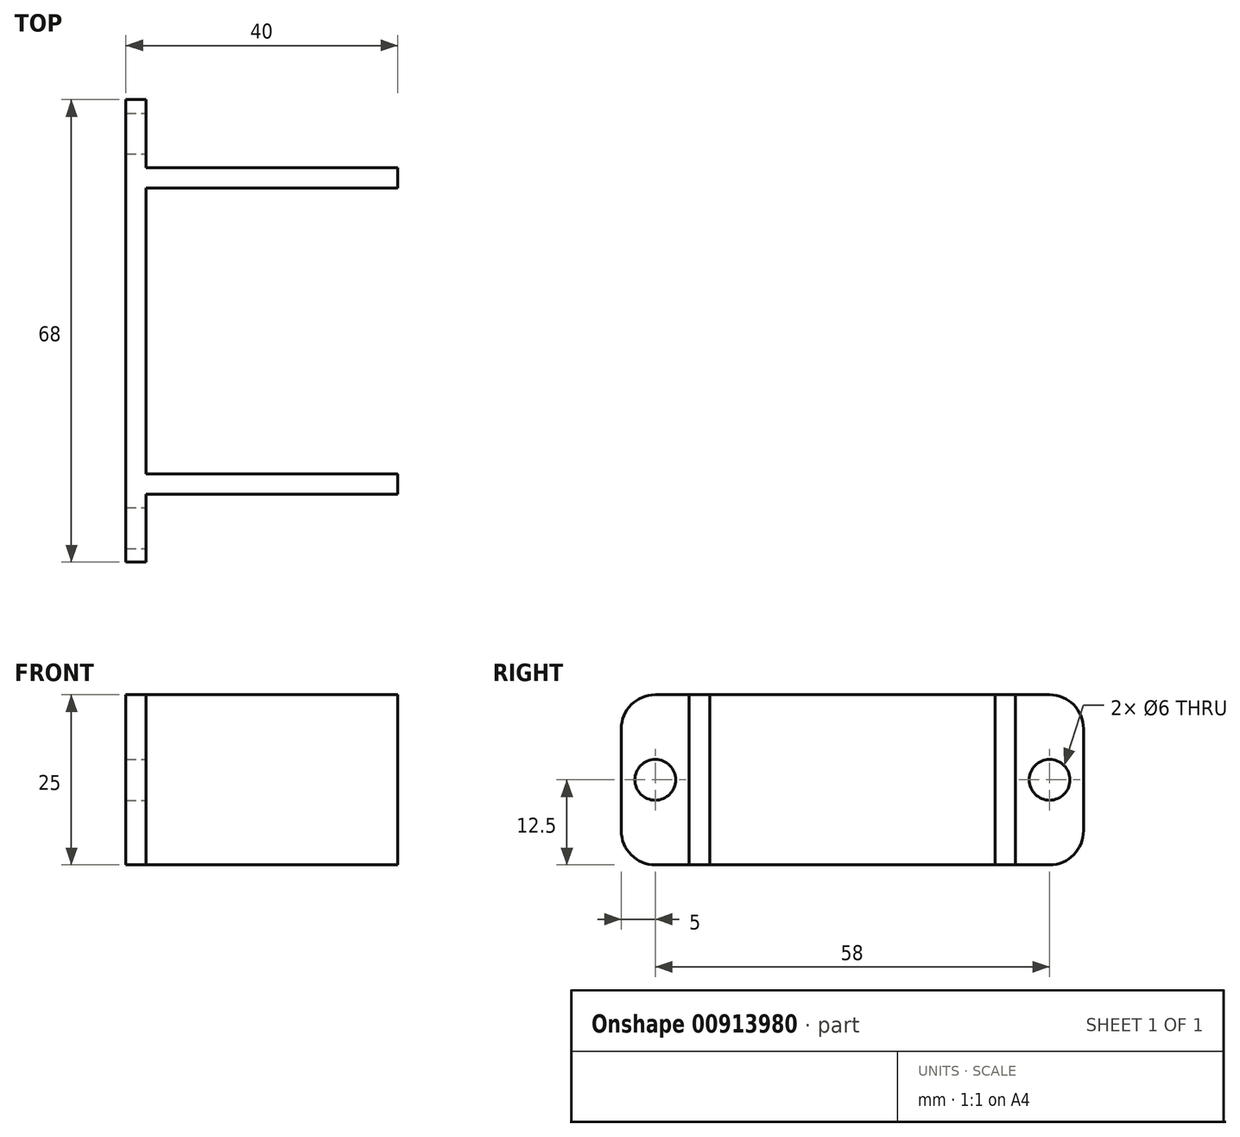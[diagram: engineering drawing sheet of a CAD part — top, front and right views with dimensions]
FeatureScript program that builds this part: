
annotation { "Feature Type Name" : "Feature", "Feature Type Description" : "" }
export const myFeature = defineFeature(function(context is Context, id is Id, definition is map)
    precondition{}
    {
        {
            var Q0;
            Q0=qCreatedBy(makeId("Top.planeOp"),FACE);
            var sketch = newSketch(context, id + "F0", { "sketchPlane" : qUnion([Q0])});
            skLineSegment(sketch, "E0.bottom", {"start": v(20, -24) * mm, "end": v(-20, -24) * mm});
            skLineSegment(sketch, "E0.top", {"start": v(20, 24) * mm, "end": v(-20, 24) * mm});
            skLineSegment(sketch, "E0.left", {"start": v(20, -24) * mm, "end": v(20, 24) * mm});
            skLineSegment(sketch, "E0.right", {"start": v(-20, -24) * mm, "end": v(-20, 24) * mm});
            skPoint(sketch, "E0.middle", {"position": v(0, 0) * mm});
            skSolve(sketch);
        }
        {
            var Q0;
            Q0=makeQuery(id+"F0.imprint","IMPRINT",FACE,{"disambiguationData":[TD([[makeQuery(id+"F0.imprint","IMPRINT",EDGE,{"derivedFrom":sQuery(id+"F0.wireOp",EDGE,"E0.bottom")}),-1.0]])]});
            extrude(context, id + "F1", {"entities" : qUnion([Q0]), "depth" : 25 * mm, "offsetDistance" : 25 * mm});
        }
        {
            var Q0;
            Q0=makeQuery(id+"F1.opExtrude","SWEPT_FACE",FACE,{"disambiguationData":[OSD([sQuery(id+"F0.wireOp",EDGE,"E0.bottom")])]});
            var sketch = newSketch(context, id + "F2", { "sketchPlane" : qUnion([Q0])});
            skLineSegment(sketch, "E1", {"start": v(-20, 25) * mm, "end": v(-17, 25) * mm});
            skLineSegment(sketch, "E2", {"start": v(-17, 25) * mm, "end": v(-17, 0) * mm});
            skLineSegment(sketch, "E3", {"start": v(20, 25) * mm, "end": v(17, 25) * mm});
            skLineSegment(sketch, "E4", {"start": v(17, 25) * mm, "end": v(17, 0) * mm});
            skSolve(sketch);
        }
        {
            var Q0;
            Q0=makeQuery(id+"F1.opExtrude","SWEPT_FACE",FACE,{"disambiguationData":[OSD([sQuery(id+"F0.wireOp",EDGE,"E0.left")])]});
            var sketch = newSketch(context, id + "F3", { "sketchPlane" : qUnion([Q0])});
            skLineSegment(sketch, "E5", {"start": v(-24, 25) * mm, "end": v(-21, 25) * mm});
            skLineSegment(sketch, "E6", {"start": v(-21, 25) * mm, "end": v(-21, 0) * mm});
            skLineSegment(sketch, "E7", {"start": v(24, 25) * mm, "end": v(21, 25) * mm});
            skLineSegment(sketch, "E8", {"start": v(21, 25) * mm, "end": v(21, 0) * mm});
            skSolve(sketch);
        }
        {
            var Q0;
            {var subQ0=sQuery(id+"F3.wireOp",EDGE,"E6");Q0=makeQuery(id+"F3.imprint","IMPRINT",FACE,{"disambiguationData":[TD([[makeQuery(id+"F3.imprint","IMPRINT",EDGE,{"derivedFrom":subQ0}),1.0]])]});}
            extrude(context, id + "F4", {"entities" : qUnion([Q0]), "operationType" : NewBodyOperationType.REMOVE, "oppositeDirection" : true, "depth" : 37 * mm, "offsetDistance" : 25 * mm});
        }
        {
            var Q0;
            Q0=makeQuery(id+"F2.imprint","IMPRINT",FACE,{"disambiguationData":[TD([[makeQuery(id+"F2.imprint","IMPRINT",EDGE,{"derivedFrom":sQuery(id+"F2.wireOp",EDGE,"E1")}),1.0]])]});
            extrude(context, id + "F5", {"entities" : qUnion([Q0]), "operationType" : NewBodyOperationType.ADD, "depth" : 10 * mm, "offsetDistance" : 25 * mm});
        }
        {
            var Q0;
            Q0=makeQuery(id+"F1.opExtrude","SWEPT_FACE",FACE,{"disambiguationData":[OSD([sQuery(id+"F0.wireOp",EDGE,"E0.top")])]});
            var sketch = newSketch(context, id + "F6", { "sketchPlane" : qUnion([Q0])});
            skLineSegment(sketch, "E9", {"start": v(20, 0) * mm, "end": v(17, 0) * mm});
            skLineSegment(sketch, "E10", {"start": v(17, 0) * mm, "end": v(17, 25) * mm});
            skSolve(sketch);
        }
        {
            var Q0;
            Q0=makeQuery(id+"F6.imprint","IMPRINT",FACE,{"disambiguationData":[TD([[makeQuery(id+"F6.imprint","IMPRINT",EDGE,{"derivedFrom":sQuery(id+"F6.wireOp",EDGE,"E9")}),1.0]])]});
            extrude(context, id + "F7", {"entities" : qUnion([Q0]), "operationType" : NewBodyOperationType.ADD, "depth" : 10 * mm, "offsetDistance" : 25 * mm});
        }
        {
            var Q0;
            Q0=makeQuery(id+"F7.opExtrude","CAP_EDGE",EDGE,{"disambiguationData":[OSD([sQuery(id+"F6.wireOp",EDGE,"E9")])],"isStart":false});
            var Q1;
            Q1=makeQuery(id+"F7.opExtrude","CAP_EDGE",EDGE,{"disambiguationData":[OSD([sQuery(id+"F0.wireOp",EDGE,"E0.top")])],"isStart":false});
            var Q2;
            Q2=makeQuery(id+"F5.opExtrude","CAP_EDGE",EDGE,{"disambiguationData":[OSD([sQuery(id+"F0.wireOp",EDGE,"E0.bottom")])],"isStart":false});
            var Q3;
            Q3=makeQuery(id+"F5.opExtrude","CAP_EDGE",EDGE,{"disambiguationData":[OSD([sQuery(id+"F2.wireOp",EDGE,"E1")])],"isStart":false});
            fillet(context, id + "F8", {"entities" : qUnion([Q0, Q1, Q2, Q3]), "radius" : 5 * mm, "tangentPropagation" : true, "allowEdgeOverflow" : false});
        }
        {
            var Q0;
            Q0=makeQuery(id+"F5.opExtrude","SWEPT_FACE",FACE,{"disambiguationData":[OSD([sQuery(id+"F2.wireOp",EDGE,"E2")])]});
            var sketch = newSketch(context, id + "F9", { "sketchPlane" : qUnion([Q0])});
            skLineSegment(sketch, "E11", {"start": v(-29, 0) * mm, "end": v(-29, 25) * mm});
            skCircle(sketch, "E12", {"center": v(-29, 12.5) * mm, "radius": 3 * mm});
            skSolve(sketch);
        }
        {
            var Q0;
            Q0=makeQuery(id+"F7.opExtrude","SWEPT_FACE",FACE,{"disambiguationData":[OSD([sQuery(id+"F6.wireOp",EDGE,"E10")])]});
            var sketch = newSketch(context, id + "F10", { "sketchPlane" : qUnion([Q0])});
            skLineSegment(sketch, "E13", {"start": v(29, 0) * mm, "end": v(29, 25) * mm});
            skCircle(sketch, "E14", {"center": v(29, 12.5) * mm, "radius": 3 * mm});
            skSolve(sketch);
        }
        {
            var Q0;
            {var subQ0=sQuery(id+"F10.wireOp",EDGE,"E14");var subQ1=sQuery(id+"F10.wireOp",EDGE,"E13");var subQ2=makeQuery(id+"F10.imprint","INTERSECT",VERTEX,{"disambiguationData":[OD(0.0)],"derivedFrom":[subQ1,subQ0]});Q0=makeQuery(id+"F10.imprint","IMPRINT",FACE,{"disambiguationData":[TD([[makeQuery(id+"F10.imprint","IMPRINT",EDGE,{"disambiguationData":[TD([[subQ2,-1.0]])],"derivedFrom":subQ1}),1.0]])]});}
            var Q1;
            {var subQ0=sQuery(id+"F10.wireOp",EDGE,"E14");var subQ1=sQuery(id+"F10.wireOp",EDGE,"E13");var subQ2=makeQuery(id+"F10.imprint","INTERSECT",VERTEX,{"disambiguationData":[OD(0.0)],"derivedFrom":[subQ1,subQ0]});Q1=makeQuery(id+"F10.imprint","IMPRINT",FACE,{"disambiguationData":[TD([[makeQuery(id+"F10.imprint","IMPRINT",EDGE,{"disambiguationData":[TD([[subQ2,-1.0]])],"derivedFrom":subQ1}),-1.0]])]});}
            var Q2;
            {var subQ0=sQuery(id+"F9.wireOp",EDGE,"E12");var subQ1=sQuery(id+"F9.wireOp",EDGE,"E11");var subQ2=makeQuery(id+"F9.imprint","INTERSECT",VERTEX,{"disambiguationData":[OD(0.0)],"derivedFrom":[subQ1,subQ0]});Q2=makeQuery(id+"F9.imprint","IMPRINT",FACE,{"disambiguationData":[TD([[makeQuery(id+"F9.imprint","IMPRINT",EDGE,{"disambiguationData":[TD([[subQ2,-1.0]])],"derivedFrom":subQ1}),1.0]])]});}
            var Q3;
            {var subQ0=sQuery(id+"F9.wireOp",EDGE,"E12");var subQ1=sQuery(id+"F9.wireOp",EDGE,"E11");var subQ2=makeQuery(id+"F9.imprint","INTERSECT",VERTEX,{"disambiguationData":[OD(0.0)],"derivedFrom":[subQ1,subQ0]});Q3=makeQuery(id+"F9.imprint","IMPRINT",FACE,{"disambiguationData":[TD([[makeQuery(id+"F9.imprint","IMPRINT",EDGE,{"disambiguationData":[TD([[subQ2,-1.0]])],"derivedFrom":subQ1}),-1.0]])]});}
            extrude(context, id + "F11", {"entities" : qUnion([Q0, Q1, Q2, Q3]), "operationType" : NewBodyOperationType.REMOVE, "oppositeDirection" : true, "depth" : 25 * mm, "offsetDistance" : 25 * mm});
        }
    });
